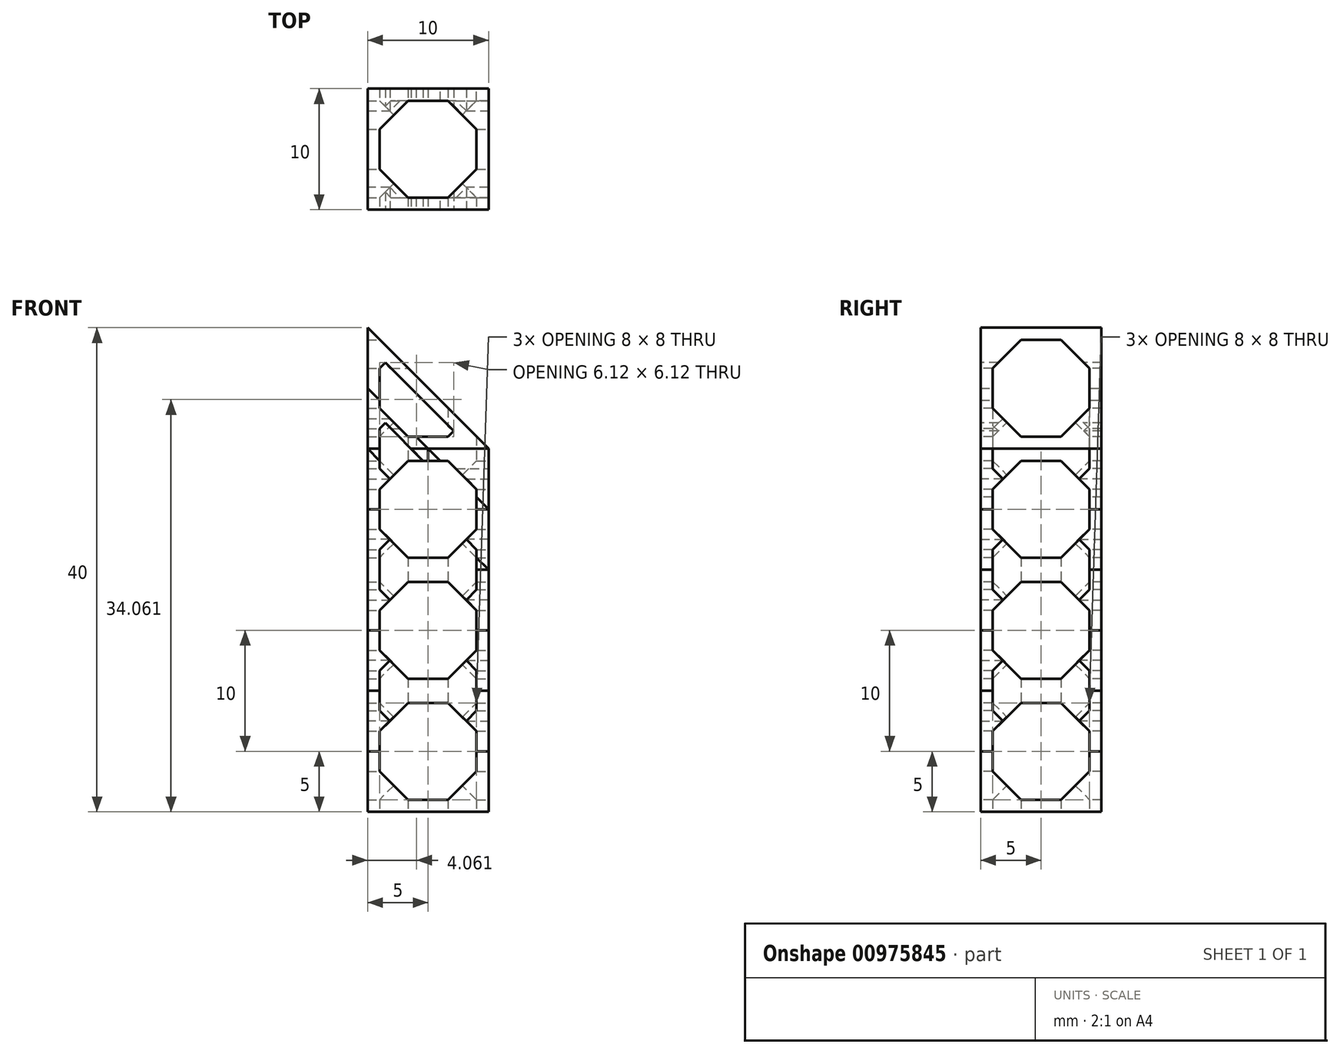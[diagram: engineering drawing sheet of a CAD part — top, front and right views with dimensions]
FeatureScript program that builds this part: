
annotation { "Feature Type Name" : "Feature", "Feature Type Description" : "" }
export const myFeature = defineFeature(function(context is Context, id is Id, definition is map)
    precondition{}
    {
        {
            var Q0;
            Q0=qCreatedBy(makeId("Front.planeOp"),FACE);
            var sketch = newSketch(context, id + "F0", { "sketchPlane" : qUnion([Q0])});
            skLineSegment(sketch, "E0.bottom", {"start": v(-5, 5) * mm, "end": v(5, 5) * mm});
            skLineSegment(sketch, "E0.top", {"start": v(-5, -5) * mm, "end": v(5, -5) * mm});
            skLineSegment(sketch, "E0.left", {"start": v(-5, 5) * mm, "end": v(-5, -5) * mm});
            skLineSegment(sketch, "E0.right", {"start": v(5, 5) * mm, "end": v(5, -5) * mm});
            skPoint(sketch, "E0.middle", {"position": v(0, 0) * mm});
            skSolve(sketch);
        }
        {
            var Q0;
            Q0=qSketchRegion(id+"F0",true);
            extrude(context, id + "F1", {"entities" : qUnion([Q0]), "endBound" : BoundingType.SYMMETRIC, "depth" : 10 * mm, "offsetDistance" : 25 * mm});
        }
        {
            var Q0;
            Q0=makeQuery(id+"F1.opExtrude","CAP_FACE",FACE,{"disambiguationData":[OSD([sQuery(id+"F0.wireOp",EDGE,"E0.bottom"),sQuery(id+"F0.wireOp",EDGE,"E0.top"),sQuery(id+"F0.wireOp",EDGE,"E0.left"),sQuery(id+"F0.wireOp",EDGE,"E0.right")])],"isStart":false});
            var sketch = newSketch(context, id + "F2", { "sketchPlane" : qUnion([Q0])});
            skCircle(sketch, "E1.cCircle", {"center": v(0, 0) * mm, "radius": 4 * mm, "construction": true});
            skLineSegment(sketch, "E1.0", {"start": v(1.66, 4) * mm, "end": v(4, 1.66) * mm});
            skLineSegment(sketch, "E1.1", {"start": v(4, 1.66) * mm, "end": v(4, -1.66) * mm});
            skLineSegment(sketch, "E1.2", {"start": v(4, -1.66) * mm, "end": v(1.66, -4) * mm});
            skLineSegment(sketch, "E1.3", {"start": v(1.66, -4) * mm, "end": v(-1.66, -4) * mm});
            skLineSegment(sketch, "E1.4", {"start": v(-1.66, -4) * mm, "end": v(-4, -1.66) * mm});
            skLineSegment(sketch, "E1.5", {"start": v(-4, -1.66) * mm, "end": v(-4, 1.66) * mm});
            skLineSegment(sketch, "E1.6", {"start": v(-4, 1.66) * mm, "end": v(-1.66, 4) * mm});
            skLineSegment(sketch, "E1.7", {"start": v(-1.66, 4) * mm, "end": v(1.66, 4) * mm});
            skPoint(sketch, "E1.0.midPoint", {"position": v(2.83, 2.83) * mm});
            skSolve(sketch);
        }
        {
            var Q0;
            Q0 = qSketchRegion(id + "F2", true);
            var Q1;
            Q1=makeQuery(id+"F1.opExtrude","CAP_FACE",FACE,{"disambiguationData":[OSD([sQuery(id+"F0.wireOp",EDGE,"E0.bottom"),sQuery(id+"F0.wireOp",EDGE,"E0.top"),sQuery(id+"F0.wireOp",EDGE,"E0.left"),sQuery(id+"F0.wireOp",EDGE,"E0.right")])],"isStart":true});
            extrude(context, id + "F3", {"entities" : qUnion([Q0]), "operationType" : NewBodyOperationType.REMOVE, "endBound" : BoundingType.UP_TO_SURFACE, "oppositeDirection" : true, "depth" : 25 * mm, "endBoundEntityFace" : qUnion([Q1]), "offsetDistance" : 25 * mm});
        }
        {
            var Q0;
            Q0=makeQuery(id+"F1.opExtrude","SWEPT_FACE",FACE,{"disambiguationData":[OSD([sQuery(id+"F0.wireOp",EDGE,"E0.right")])]});
            var sketch = newSketch(context, id + "F4", { "sketchPlane" : qUnion([Q0])});
            skCircle(sketch, "E2.cCircle", {"center": v(0, 0) * mm, "radius": 4 * mm, "construction": true});
            skLineSegment(sketch, "E2.0", {"start": v(-4, 1.66) * mm, "end": v(-1.66, 4) * mm});
            skLineSegment(sketch, "E2.1", {"start": v(-1.66, 4) * mm, "end": v(1.66, 4) * mm});
            skLineSegment(sketch, "E2.2", {"start": v(1.66, 4) * mm, "end": v(4, 1.66) * mm});
            skLineSegment(sketch, "E2.3", {"start": v(4, 1.66) * mm, "end": v(4, -1.66) * mm});
            skLineSegment(sketch, "E2.4", {"start": v(4, -1.66) * mm, "end": v(1.66, -4) * mm});
            skLineSegment(sketch, "E2.5", {"start": v(1.66, -4) * mm, "end": v(-1.66, -4) * mm});
            skLineSegment(sketch, "E2.6", {"start": v(-1.66, -4) * mm, "end": v(-4, -1.66) * mm});
            skLineSegment(sketch, "E2.7", {"start": v(-4, -1.66) * mm, "end": v(-4, 1.66) * mm});
            skPoint(sketch, "E2.0.midPoint", {"position": v(-2.83, 2.83) * mm});
            skSolve(sketch);
        }
        {
            var Q0;
            Q0 = qSketchRegion(id + "F4", true);
            var Q1;
            Q1 = qConstructionFilter(qBodyType(qCreatedBy(id + "F4" ,EDGE), BodyType.WIRE), ConstructionObject.NO);
            var Q2;
            Q2=makeQuery(id+"F1.opExtrude","SWEPT_FACE",FACE,{"disambiguationData":[OSD([sQuery(id+"F0.wireOp",EDGE,"E0.left")])]});
            extrude(context, id + "F5", {"entities" : qUnion([Q0]), "operationType" : NewBodyOperationType.REMOVE, "surfaceEntities" : qUnion([Q1]), "endBound" : BoundingType.UP_TO_SURFACE, "oppositeDirection" : true, "depth" : 25 * mm, "endBoundEntityFace" : qUnion([Q2]), "offsetDistance" : 25 * mm});
        }
        {
            var Q0;
            Q0=makeQuery(id+"F1.opExtrude","SWEPT_FACE",FACE,{"disambiguationData":[OSD([sQuery(id+"F0.wireOp",EDGE,"E0.bottom")])]});
            var sketch = newSketch(context, id + "F6", { "sketchPlane" : qUnion([Q0])});
            skCircle(sketch, "E3.cCircle", {"center": v(0, 0) * mm, "radius": 4 * mm, "construction": true});
            skLineSegment(sketch, "E3.0", {"start": v(-4, 1.66) * mm, "end": v(-1.66, 4) * mm});
            skLineSegment(sketch, "E3.1", {"start": v(-1.66, 4) * mm, "end": v(1.66, 4) * mm});
            skLineSegment(sketch, "E3.2", {"start": v(1.66, 4) * mm, "end": v(4, 1.66) * mm});
            skLineSegment(sketch, "E3.3", {"start": v(4, 1.66) * mm, "end": v(4, -1.66) * mm});
            skLineSegment(sketch, "E3.4", {"start": v(4, -1.66) * mm, "end": v(1.66, -4) * mm});
            skLineSegment(sketch, "E3.5", {"start": v(1.66, -4) * mm, "end": v(-1.66, -4) * mm});
            skLineSegment(sketch, "E3.6", {"start": v(-1.66, -4) * mm, "end": v(-4, -1.66) * mm});
            skLineSegment(sketch, "E3.7", {"start": v(-4, -1.66) * mm, "end": v(-4, 1.66) * mm});
            skPoint(sketch, "E3.0.midPoint", {"position": v(-2.83, 2.83) * mm});
            skSolve(sketch);
        }
        {
            var Q0;
            Q0 = qSketchRegion(id + "F6", true);
            var Q1;
            Q1=makeQuery(id+"F1.opExtrude","SWEPT_FACE",FACE,{"disambiguationData":[OSD([sQuery(id+"F0.wireOp",EDGE,"E0.top")])]});
            extrude(context, id + "F7", {"entities" : qUnion([Q0]), "operationType" : NewBodyOperationType.REMOVE, "endBound" : BoundingType.UP_TO_SURFACE, "oppositeDirection" : true, "depth" : 25 * mm, "endBoundEntityFace" : qUnion([Q1]), "offsetDistance" : 25 * mm});
        }
        {
            var Q0;
            Q0=qCreatedBy(makeId("Front.planeOp"),FACE);
            var sketch = newSketch(context, id + "F8", { "sketchPlane" : qUnion([Q0])});
            skLineSegment(sketch, "E4.bottom", {"start": v(-5, 10) * mm, "end": v(5, 10) * mm});
            skLineSegment(sketch, "E4.top", {"start": v(-5, -10) * mm, "end": v(5, -10) * mm});
            skLineSegment(sketch, "E4.left", {"start": v(-5, 10) * mm, "end": v(-5, -10) * mm});
            skLineSegment(sketch, "E4.right", {"start": v(5, 10) * mm, "end": v(5, -10) * mm});
            skPoint(sketch, "E4.middle", {"position": v(0, 0) * mm});
            skSolve(sketch);
        }
        {
            var Q0;
            Q0=qSketchRegion(id+"F8",true);
            extrude(context, id + "F9", {"entities" : qUnion([Q0]), "endBound" : BoundingType.SYMMETRIC, "depth" : 10 * mm, "offsetDistance" : 25 * mm});
        }
        {
            var Q0;
            Q0=makeQuery(id+"F9.opExtrude","CAP_FACE",FACE,{"disambiguationData":[OSD([sQuery(id+"F8.wireOp",EDGE,"E4.bottom"),sQuery(id+"F8.wireOp",EDGE,"E4.top"),sQuery(id+"F8.wireOp",EDGE,"E4.left"),sQuery(id+"F8.wireOp",EDGE,"E4.right")])],"isStart":false});
            var sketch = newSketch(context, id + "F10", { "sketchPlane" : qUnion([Q0])});
            skLineSegment(sketch, "E5", {"start": v(-5, 0) * mm, "end": v(5, 0) * mm, "construction": true});
            skLineSegment(sketch, "E6", {"start": v(-5, -10) * mm, "end": v(-5, 0) * mm, "construction": true});
            skLineSegment(sketch, "E7", {"start": v(-5, 10) * mm, "end": v(-5, 0) * mm, "construction": true});
            skCircle(sketch, "E8.cCircle", {"center": v(0, 5) * mm, "radius": 4 * mm, "construction": true});
            skPoint(sketch, "E8.cCircle.centerSnap0", {"position": v(-5, 5) * mm});
            skLineSegment(sketch, "E8.0", {"start": v(4, 6.66) * mm, "end": v(4, 3.34) * mm});
            skLineSegment(sketch, "E8.1", {"start": v(4, 3.34) * mm, "end": v(1.66, 1) * mm});
            skLineSegment(sketch, "E8.2", {"start": v(1.66, 1) * mm, "end": v(-1.66, 1) * mm});
            skLineSegment(sketch, "E8.3", {"start": v(-1.66, 1) * mm, "end": v(-4, 3.34) * mm});
            skLineSegment(sketch, "E8.4", {"start": v(-4, 3.34) * mm, "end": v(-4, 6.66) * mm});
            skLineSegment(sketch, "E8.5", {"start": v(-4, 6.66) * mm, "end": v(-1.66, 9) * mm});
            skLineSegment(sketch, "E8.6", {"start": v(-1.66, 9) * mm, "end": v(1.66, 9) * mm});
            skLineSegment(sketch, "E8.7", {"start": v(1.66, 9) * mm, "end": v(4, 6.66) * mm});
            skPoint(sketch, "E8.0.midPoint", {"position": v(4, 5) * mm});
            skCircle(sketch, "E9.cCircle", {"center": v(0, -5) * mm, "radius": 4 * mm, "construction": true});
            skPoint(sketch, "E9.cCircle.centerSnap0", {"position": v(-5, -5) * mm});
            skPoint(sketch, "E9.cCircle.centerSnap1", {"position": v(0, 1) * mm});
            skLineSegment(sketch, "E9.0", {"start": v(4, -3.34) * mm, "end": v(4, -6.66) * mm});
            skLineSegment(sketch, "E9.1", {"start": v(4, -6.66) * mm, "end": v(1.66, -9) * mm});
            skLineSegment(sketch, "E9.2", {"start": v(1.66, -9) * mm, "end": v(-1.66, -9) * mm});
            skLineSegment(sketch, "E9.3", {"start": v(-1.66, -9) * mm, "end": v(-4, -6.66) * mm});
            skLineSegment(sketch, "E9.4", {"start": v(-4, -6.66) * mm, "end": v(-4, -3.34) * mm});
            skLineSegment(sketch, "E9.5", {"start": v(-4, -3.34) * mm, "end": v(-1.66, -1) * mm});
            skLineSegment(sketch, "E9.6", {"start": v(-1.66, -1) * mm, "end": v(1.66, -1) * mm});
            skLineSegment(sketch, "E9.7", {"start": v(1.66, -1) * mm, "end": v(4, -3.34) * mm});
            skPoint(sketch, "E9.0.midPoint", {"position": v(4, -5) * mm});
            skSolve(sketch);
        }
        {
            var Q0;
            Q0 = qSketchRegion(id + "F10", true);
            var Q1;
            Q1=makeQuery(id+"F9.opExtrude","CAP_FACE",FACE,{"disambiguationData":[OSD([sQuery(id+"F8.wireOp",EDGE,"E4.bottom"),sQuery(id+"F8.wireOp",EDGE,"E4.top"),sQuery(id+"F8.wireOp",EDGE,"E4.left"),sQuery(id+"F8.wireOp",EDGE,"E4.right")])],"isStart":true});
            extrude(context, id + "F11", {"entities" : qUnion([Q0]), "operationType" : NewBodyOperationType.REMOVE, "endBound" : BoundingType.UP_TO_SURFACE, "oppositeDirection" : true, "depth" : 25 * mm, "endBoundEntityFace" : qUnion([Q1]), "offsetDistance" : 25 * mm});
        }
        {
            var Q0;
            Q0=makeQuery(id+"F9.opExtrude","SWEPT_FACE",FACE,{"disambiguationData":[OSD([sQuery(id+"F8.wireOp",EDGE,"E4.right")])]});
            var sketch = newSketch(context, id + "F12", { "sketchPlane" : qUnion([Q0])});
            skLineSegment(sketch, "E10", {"start": v(-5, 0) * mm, "end": v(5, 0) * mm, "construction": true});
            skLineSegment(sketch, "E11", {"start": v(-5, 10) * mm, "end": v(-5, 0) * mm, "construction": true});
            skLineSegment(sketch, "E12", {"start": v(-5, 0) * mm, "end": v(-5, -10) * mm, "construction": true});
            skCircle(sketch, "E13.cCircle", {"center": v(0, 5) * mm, "radius": 4 * mm, "construction": true});
            skPoint(sketch, "E13.cCircle.centerSnap0", {"position": v(-5, 5) * mm});
            skLineSegment(sketch, "E13.0", {"start": v(4, 6.66) * mm, "end": v(4, 3.34) * mm});
            skLineSegment(sketch, "E13.1", {"start": v(4, 3.34) * mm, "end": v(1.66, 1) * mm});
            skLineSegment(sketch, "E13.2", {"start": v(1.66, 1) * mm, "end": v(-1.66, 1) * mm});
            skLineSegment(sketch, "E13.3", {"start": v(-1.66, 1) * mm, "end": v(-4, 3.34) * mm});
            skLineSegment(sketch, "E13.4", {"start": v(-4, 3.34) * mm, "end": v(-4, 6.66) * mm});
            skLineSegment(sketch, "E13.5", {"start": v(-4, 6.66) * mm, "end": v(-1.66, 9) * mm});
            skLineSegment(sketch, "E13.6", {"start": v(-1.66, 9) * mm, "end": v(1.66, 9) * mm});
            skLineSegment(sketch, "E13.7", {"start": v(1.66, 9) * mm, "end": v(4, 6.66) * mm});
            skPoint(sketch, "E13.0.midPoint", {"position": v(4, 5) * mm});
            skCircle(sketch, "E14.cCircle", {"center": v(0, -5) * mm, "radius": 4 * mm, "construction": true});
            skPoint(sketch, "E14.cCircle.centerSnap0", {"position": v(-5, -5) * mm});
            skPoint(sketch, "E14.cCircle.centerSnap1", {"position": v(0, 1) * mm});
            skLineSegment(sketch, "E14.0", {"start": v(4, -3.34) * mm, "end": v(4, -6.66) * mm});
            skLineSegment(sketch, "E14.1", {"start": v(4, -6.66) * mm, "end": v(1.66, -9) * mm});
            skLineSegment(sketch, "E14.2", {"start": v(1.66, -9) * mm, "end": v(-1.66, -9) * mm});
            skLineSegment(sketch, "E14.3", {"start": v(-1.66, -9) * mm, "end": v(-4, -6.66) * mm});
            skLineSegment(sketch, "E14.4", {"start": v(-4, -6.66) * mm, "end": v(-4, -3.34) * mm});
            skLineSegment(sketch, "E14.5", {"start": v(-4, -3.34) * mm, "end": v(-1.66, -1) * mm});
            skLineSegment(sketch, "E14.6", {"start": v(-1.66, -1) * mm, "end": v(1.66, -1) * mm});
            skLineSegment(sketch, "E14.7", {"start": v(1.66, -1) * mm, "end": v(4, -3.34) * mm});
            skPoint(sketch, "E14.0.midPoint", {"position": v(4, -5) * mm});
            skSolve(sketch);
        }
        {
            var Q0;
            Q0 = qSketchRegion(id + "F12", true);
            var Q1;
            Q1=makeQuery(id+"F9.opExtrude","SWEPT_FACE",FACE,{"disambiguationData":[OSD([sQuery(id+"F8.wireOp",EDGE,"E4.left")])]});
            extrude(context, id + "F13", {"entities" : qUnion([Q0]), "operationType" : NewBodyOperationType.REMOVE, "endBound" : BoundingType.UP_TO_SURFACE, "oppositeDirection" : true, "depth" : 25 * mm, "endBoundEntityFace" : qUnion([Q1]), "offsetDistance" : 25 * mm});
        }
        {
            var Q0;
            Q0=makeQuery(id+"F9.opExtrude","SWEPT_FACE",FACE,{"disambiguationData":[OSD([sQuery(id+"F8.wireOp",EDGE,"E4.bottom")])]});
            var sketch = newSketch(context, id + "F14", { "sketchPlane" : qUnion([Q0])});
            skCircle(sketch, "E15.cCircle", {"center": v(0, 0) * mm, "radius": 4 * mm, "construction": true});
            skLineSegment(sketch, "E15.0", {"start": v(-4, 1.66) * mm, "end": v(-1.66, 4) * mm});
            skLineSegment(sketch, "E15.1", {"start": v(-1.66, 4) * mm, "end": v(1.66, 4) * mm});
            skLineSegment(sketch, "E15.2", {"start": v(1.66, 4) * mm, "end": v(4, 1.66) * mm});
            skLineSegment(sketch, "E15.3", {"start": v(4, 1.66) * mm, "end": v(4, -1.66) * mm});
            skLineSegment(sketch, "E15.4", {"start": v(4, -1.66) * mm, "end": v(1.66, -4) * mm});
            skLineSegment(sketch, "E15.5", {"start": v(1.66, -4) * mm, "end": v(-1.66, -4) * mm});
            skLineSegment(sketch, "E15.6", {"start": v(-1.66, -4) * mm, "end": v(-4, -1.66) * mm});
            skLineSegment(sketch, "E15.7", {"start": v(-4, -1.66) * mm, "end": v(-4, 1.66) * mm});
            skPoint(sketch, "E15.0.midPoint", {"position": v(-2.83, 2.83) * mm});
            skSolve(sketch);
        }
        {
            var Q0;
            Q0 = qSketchRegion(id + "F14", true);
            var Q1;
            Q1=makeQuery(id+"F9.opExtrude","SWEPT_FACE",FACE,{"disambiguationData":[OSD([sQuery(id+"F8.wireOp",EDGE,"E4.top")])]});
            extrude(context, id + "F15", {"entities" : qUnion([Q0]), "operationType" : NewBodyOperationType.REMOVE, "endBound" : BoundingType.UP_TO_SURFACE, "oppositeDirection" : true, "depth" : 25 * mm, "endBoundEntityFace" : qUnion([Q1]), "offsetDistance" : 25 * mm});
        }
        {
            var Q0;
            Q0=qCreatedBy(makeId("Front.planeOp"),FACE);
            var sketch = newSketch(context, id + "F16", { "sketchPlane" : qUnion([Q0])});
            skLineSegment(sketch, "E16.bottom", {"start": v(-5, 10) * mm, "end": v(0, 10) * mm});
            skLineSegment(sketch, "E16.top", {"start": v(-5, -10) * mm, "end": v(5, -10) * mm});
            skLineSegment(sketch, "E16.left", {"start": v(-5, 10) * mm, "end": v(-5, -10) * mm});
            skLineSegment(sketch, "E16.right", {"start": v(5, 0) * mm, "end": v(5, -10) * mm});
            skPoint(sketch, "E16.middle", {"position": v(0, 0) * mm});
            skLineSegment(sketch, "E17", {"start": v(0, 0) * mm, "end": v(0, 10) * mm});
            skLineSegment(sketch, "E18", {"start": v(0, 0) * mm, "end": v(5, 0) * mm});
            skSolve(sketch);
        }
        {
            var Q0;
            Q0=qSketchRegion(id+"F16",true);
            extrude(context, id + "F17", {"entities" : qUnion([Q0]), "endBound" : BoundingType.SYMMETRIC, "depth" : 10 * mm, "offsetDistance" : 25 * mm});
        }
        {
            var Q0;
            Q0=makeQuery(id+"F17.opExtrude","CAP_FACE",FACE,{"disambiguationData":[OSD([sQuery(id+"F16.wireOp",EDGE,"E16.bottom"),sQuery(id+"F16.wireOp",EDGE,"E16.top"),sQuery(id+"F16.wireOp",EDGE,"E16.left"),sQuery(id+"F16.wireOp",EDGE,"E16.right"),sQuery(id+"F16.wireOp",EDGE,"E17"),sQuery(id+"F16.wireOp",EDGE,"E18")])],"isStart":false});
            var sketch = newSketch(context, id + "F18", { "sketchPlane" : qUnion([Q0])});
            skLineSegment(sketch, "E19", {"start": v(0, 0) * mm, "end": v(-5, 0) * mm, "construction": true});
            skLineSegment(sketch, "E20", {"start": v(-5, 0) * mm, "end": v(-5, 10) * mm, "construction": true});
            skLineSegment(sketch, "E21", {"start": v(-5, 0) * mm, "end": v(-5, -10) * mm, "construction": true});
            skCircle(sketch, "E22.cCircle", {"center": v(0, -5) * mm, "radius": 4 * mm, "construction": true});
            skPoint(sketch, "E22.cCircle.centerSnap0", {"position": v(-5, -5) * mm});
            skLineSegment(sketch, "E22.0", {"start": v(4, -3.34) * mm, "end": v(4, -6.66) * mm});
            skLineSegment(sketch, "E22.1", {"start": v(4, -6.66) * mm, "end": v(1.66, -9) * mm});
            skLineSegment(sketch, "E22.2", {"start": v(1.66, -9) * mm, "end": v(-1.66, -9) * mm});
            skLineSegment(sketch, "E22.3", {"start": v(-1.66, -9) * mm, "end": v(-4, -6.66) * mm});
            skLineSegment(sketch, "E22.4", {"start": v(-4, -6.66) * mm, "end": v(-4, -3.34) * mm});
            skLineSegment(sketch, "E22.5", {"start": v(-4, -3.34) * mm, "end": v(-1.66, -1) * mm});
            skLineSegment(sketch, "E22.6", {"start": v(-1.66, -1) * mm, "end": v(1.66, -1) * mm});
            skLineSegment(sketch, "E22.7", {"start": v(1.66, -1) * mm, "end": v(4, -3.34) * mm});
            skPoint(sketch, "E22.0.midPoint", {"position": v(4, -5) * mm});
            skLineSegment(sketch, "E23.MirrorCS", {"start": v(-1.66, 1) * mm, "end": v(-1, 1) * mm});
            skLineSegment(sketch, "E24.MirrorCS", {"start": v(-4, 3.34) * mm, "end": v(-1.66, 1) * mm});
            skLineSegment(sketch, "E25.MirrorCS", {"start": v(-4, 6.66) * mm, "end": v(-4, 3.34) * mm});
            skLineSegment(sketch, "E26.MirrorCS", {"start": v(-1.66, 9) * mm, "end": v(-4, 6.66) * mm});
            skLineSegment(sketch, "E27.MirrorCS", {"start": v(-1, 9) * mm, "end": v(-1.66, 9) * mm});
            skLineSegment(sketch, "E28", {"start": v(-1, 9) * mm, "end": v(-1, 1) * mm});
            skSolve(sketch);
        }
        {
            var Q0;
            Q0 = qSketchRegion(id + "F18", true);
            var Q1;
            Q1=makeQuery(id+"F17.opExtrude","CAP_FACE",FACE,{"disambiguationData":[OSD([sQuery(id+"F16.wireOp",EDGE,"E16.bottom"),sQuery(id+"F16.wireOp",EDGE,"E16.top"),sQuery(id+"F16.wireOp",EDGE,"E16.left"),sQuery(id+"F16.wireOp",EDGE,"E16.right"),sQuery(id+"F16.wireOp",EDGE,"E17"),sQuery(id+"F16.wireOp",EDGE,"E18")])],"isStart":true});
            extrude(context, id + "F19", {"entities" : qUnion([Q0]), "operationType" : NewBodyOperationType.REMOVE, "endBound" : BoundingType.UP_TO_SURFACE, "oppositeDirection" : true, "depth" : 25 * mm, "endBoundEntityFace" : qUnion([Q1]), "offsetDistance" : 25 * mm});
        }
        {
            var Q0;
            Q0=makeQuery(id+"F17.opExtrude","SWEPT_FACE",FACE,{"disambiguationData":[OSD([sQuery(id+"F16.wireOp",EDGE,"E16.right")])]});
            var sketch = newSketch(context, id + "F20", { "sketchPlane" : qUnion([Q0])});
            skLineSegment(sketch, "E29", {"start": v(-5, -10) * mm, "end": v(-5, 0) * mm, "construction": true});
            skLineSegment(sketch, "E30", {"start": v(-5, 0) * mm, "end": v(-5, 10) * mm, "construction": true});
            skCircle(sketch, "E31.cCircle", {"center": v(0, 5) * mm, "radius": 4 * mm, "construction": true});
            skPoint(sketch, "E31.cCircle.centerSnap0", {"position": v(-5, 5) * mm});
            skLineSegment(sketch, "E31.0", {"start": v(4, 6.66) * mm, "end": v(4, 3.34) * mm});
            skLineSegment(sketch, "E31.1", {"start": v(4, 3.34) * mm, "end": v(1.66, 1) * mm});
            skLineSegment(sketch, "E31.2", {"start": v(1.66, 1) * mm, "end": v(-1.66, 1) * mm});
            skLineSegment(sketch, "E31.3", {"start": v(-1.66, 1) * mm, "end": v(-4, 3.34) * mm});
            skLineSegment(sketch, "E31.4", {"start": v(-4, 3.34) * mm, "end": v(-4, 6.66) * mm});
            skLineSegment(sketch, "E31.5", {"start": v(-4, 6.66) * mm, "end": v(-1.66, 9) * mm});
            skLineSegment(sketch, "E31.6", {"start": v(-1.66, 9) * mm, "end": v(1.66, 9) * mm});
            skLineSegment(sketch, "E31.7", {"start": v(1.66, 9) * mm, "end": v(4, 6.66) * mm});
            skPoint(sketch, "E31.0.midPoint", {"position": v(4, 5) * mm});
            skCircle(sketch, "E32.cCircle", {"center": v(0, -5) * mm, "radius": 4 * mm, "construction": true});
            skPoint(sketch, "E32.cCircle.centerSnap0", {"position": v(-5, -5) * mm});
            skLineSegment(sketch, "E32.0", {"start": v(4, -3.34) * mm, "end": v(4, -6.66) * mm});
            skLineSegment(sketch, "E32.1", {"start": v(4, -6.66) * mm, "end": v(1.66, -9) * mm});
            skLineSegment(sketch, "E32.2", {"start": v(1.66, -9) * mm, "end": v(-1.66, -9) * mm});
            skLineSegment(sketch, "E32.3", {"start": v(-1.66, -9) * mm, "end": v(-4, -6.66) * mm});
            skLineSegment(sketch, "E32.4", {"start": v(-4, -6.66) * mm, "end": v(-4, -3.34) * mm});
            skLineSegment(sketch, "E32.5", {"start": v(-4, -3.34) * mm, "end": v(-1.66, -1) * mm});
            skLineSegment(sketch, "E32.6", {"start": v(-1.66, -1) * mm, "end": v(1.66, -1) * mm});
            skLineSegment(sketch, "E32.7", {"start": v(1.66, -1) * mm, "end": v(4, -3.34) * mm});
            skPoint(sketch, "E32.0.midPoint", {"position": v(4, -5) * mm});
            skSolve(sketch);
        }
        {
            var Q0;
            Q0 = qSketchRegion(id + "F20", true);
            var Q1;
            Q1=makeQuery(id+"F17.opExtrude","SWEPT_FACE",FACE,{"disambiguationData":[OSD([sQuery(id+"F16.wireOp",EDGE,"E16.left")])]});
            extrude(context, id + "F21", {"entities" : qUnion([Q0]), "operationType" : NewBodyOperationType.REMOVE, "endBound" : BoundingType.UP_TO_SURFACE, "oppositeDirection" : true, "depth" : 25 * mm, "endBoundEntityFace" : qUnion([Q1]), "offsetDistance" : 25 * mm});
        }
        {
            var Q0;
            Q0=makeQuery(id+"F17.opExtrude","SWEPT_FACE",FACE,{"disambiguationData":[OSD([sQuery(id+"F16.wireOp",EDGE,"E16.bottom")])]});
            var sketch = newSketch(context, id + "F22", { "sketchPlane" : qUnion([Q0])});
            skLineSegment(sketch, "E33.0", {"start": v(-4, -1.66) * mm, "end": v(-4, 1.66) * mm});
            skLineSegment(sketch, "E33.1", {"start": v(-4, 1.66) * mm, "end": v(-1.66, 4) * mm});
            skLineSegment(sketch, "E33.2", {"start": v(-1.66, 4) * mm, "end": v(-1, 4) * mm});
            skLineSegment(sketch, "E33.7", {"start": v(-1.66, -4) * mm, "end": v(-4, -1.66) * mm});
            skPoint(sketch, "E33.0.midPoint", {"position": v(-4, 0) * mm});
            skLineSegment(sketch, "E34", {"start": v(-1, -4) * mm, "end": v(-1.66, -4) * mm});
            skLineSegment(sketch, "E35", {"start": v(-1, 4) * mm, "end": v(-1, -4) * mm});
            skLineSegment(sketch, "E36", {"start": v(0, 5) * mm, "end": v(0, -5) * mm, "construction": true});
            skLineSegment(sketch, "E37.MirrorCS", {"start": v(1, 4) * mm, "end": v(1, -4) * mm});
            skLineSegment(sketch, "E38.MirrorCS", {"start": v(1.66, 4) * mm, "end": v(1, 4) * mm});
            skLineSegment(sketch, "E39.MirrorCS", {"start": v(4, 1.66) * mm, "end": v(1.66, 4) * mm});
            skLineSegment(sketch, "E40.MirrorCS", {"start": v(4, -1.66) * mm, "end": v(4, 1.66) * mm});
            skLineSegment(sketch, "E41.MirrorCS", {"start": v(1.66, -4) * mm, "end": v(4, -1.66) * mm});
            skLineSegment(sketch, "E42.MirrorCS", {"start": v(1, -4) * mm, "end": v(1.66, -4) * mm});
            skSolve(sketch);
        }
        {
            var Q0;
            Q0 = qSketchRegion(id + "F22", true);
            extrude(context, id + "F23", {"entities" : qUnion([Q0]), "operationType" : NewBodyOperationType.REMOVE, "oppositeDirection" : true, "depth" : 15 * mm, "offsetDistance" : 25 * mm});
        }
        {
            var Q0;
            Q0=makeQuery(id+"F17.opExtrude","SWEPT_FACE",FACE,{"disambiguationData":[OSD([sQuery(id+"F16.wireOp",EDGE,"E16.top")])]});
            var sketch = newSketch(context, id + "F24", { "sketchPlane" : qUnion([Q0])});
            skCircle(sketch, "E43.cCircle", {"center": v(0, 0) * mm, "radius": 4 * mm, "construction": true});
            skLineSegment(sketch, "E43.0", {"start": v(4, 1.66) * mm, "end": v(4, -1.66) * mm});
            skLineSegment(sketch, "E43.1", {"start": v(4, -1.66) * mm, "end": v(1.66, -4) * mm});
            skLineSegment(sketch, "E43.2", {"start": v(1.66, -4) * mm, "end": v(-1.66, -4) * mm});
            skLineSegment(sketch, "E43.3", {"start": v(-1.66, -4) * mm, "end": v(-4, -1.66) * mm});
            skLineSegment(sketch, "E43.4", {"start": v(-4, -1.66) * mm, "end": v(-4, 1.66) * mm});
            skLineSegment(sketch, "E43.5", {"start": v(-4, 1.66) * mm, "end": v(-1.66, 4) * mm});
            skLineSegment(sketch, "E43.6", {"start": v(-1.66, 4) * mm, "end": v(1.66, 4) * mm});
            skLineSegment(sketch, "E43.7", {"start": v(1.66, 4) * mm, "end": v(4, 1.66) * mm});
            skPoint(sketch, "E43.0.midPoint", {"position": v(4, 0) * mm});
            skSolve(sketch);
        }
        {
            var Q0;
            Q0 = qSketchRegion(id + "F24", true);
            extrude(context, id + "F25", {"entities" : qUnion([Q0]), "operationType" : NewBodyOperationType.REMOVE, "oppositeDirection" : true, "depth" : 5 * mm, "offsetDistance" : 25 * mm});
        }
        {
            var Q0;
            Q0=qCreatedBy(makeId("Front.planeOp"),FACE);
            var sketch = newSketch(context, id + "F26", { "sketchPlane" : qUnion([Q0])});
            skLineSegment(sketch, "E44.top", {"start": v(5, -10) * mm, "end": v(-5, -10) * mm});
            skLineSegment(sketch, "E44.left", {"start": v(5, 0) * mm, "end": v(5, -10) * mm});
            skLineSegment(sketch, "E44.right", {"start": v(-5, 10) * mm, "end": v(-5, -10) * mm});
            skPoint(sketch, "E44.middle", {"position": v(0, 0) * mm});
            skLineSegment(sketch, "E45", {"start": v(-5, 10) * mm, "end": v(5, 0) * mm});
            skSolve(sketch);
        }
        {
            var Q0;
            Q0=qSketchRegion(id+"F26",true);
            extrude(context, id + "F27", {"entities" : qUnion([Q0]), "endBound" : BoundingType.SYMMETRIC, "depth" : 10 * mm, "offsetDistance" : 25 * mm});
        }
        {
            var Q0;
            Q0=makeQuery(id+"F27.opExtrude","CAP_FACE",FACE,{"disambiguationData":[OSD([sQuery(id+"F26.wireOp",EDGE,"E44.top"),sQuery(id+"F26.wireOp",EDGE,"E44.left"),sQuery(id+"F26.wireOp",EDGE,"E44.right"),sQuery(id+"F26.wireOp",EDGE,"E45")])],"isStart":false});
            var sketch = newSketch(context, id + "F28", { "sketchPlane" : qUnion([Q0])});
            skLineSegment(sketch, "E46", {"start": v(-5, 0) * mm, "end": v(5, 0) * mm, "construction": true});
            skLineSegment(sketch, "E47", {"start": v(-5, 0) * mm, "end": v(-5, -10) * mm, "construction": true});
            skCircle(sketch, "E48.cCircle", {"center": v(0, -5) * mm, "radius": 4 * mm, "construction": true});
            skPoint(sketch, "E48.cCircle.centerSnap0", {"position": v(-5, -5) * mm});
            skPoint(sketch, "E48.cCircle.centerSnap1", {"position": v(0, 0) * mm});
            skLineSegment(sketch, "E48.0", {"start": v(4, -3.34) * mm, "end": v(4, -6.66) * mm});
            skLineSegment(sketch, "E48.1", {"start": v(4, -6.66) * mm, "end": v(1.66, -9) * mm});
            skLineSegment(sketch, "E48.2", {"start": v(1.66, -9) * mm, "end": v(-1.66, -9) * mm});
            skLineSegment(sketch, "E48.3", {"start": v(-1.66, -9) * mm, "end": v(-4, -6.66) * mm});
            skLineSegment(sketch, "E48.4", {"start": v(-4, -6.66) * mm, "end": v(-4, -3.34) * mm});
            skLineSegment(sketch, "E48.5", {"start": v(-4, -3.34) * mm, "end": v(-1.66, -1) * mm});
            skLineSegment(sketch, "E48.6", {"start": v(-1.66, -1) * mm, "end": v(1.66, -1) * mm});
            skLineSegment(sketch, "E48.7", {"start": v(1.66, -1) * mm, "end": v(4, -3.34) * mm});
            skPoint(sketch, "E48.0.midPoint", {"position": v(4, -5) * mm});
            skLineSegment(sketch, "E49", {"start": v(-5, 0) * mm, "end": v(-5, 10) * mm, "construction": true});
            skLineSegment(sketch, "E50.2", {"start": v(1.66, 1) * mm, "end": v(-1.66, 1) * mm});
            skLineSegment(sketch, "E50.3", {"start": v(-1.66, 1) * mm, "end": v(-4, 3.34) * mm});
            skLineSegment(sketch, "E50.4", {"start": v(-4, 3.34) * mm, "end": v(-4, 6.66) * mm});
            skLineSegment(sketch, "E50.5", {"start": v(-4, 6.66) * mm, "end": v(-3.54, 7.12) * mm});
            skLineSegment(sketch, "E51", {"start": v(2.12, 1.46) * mm, "end": v(1.66, 1) * mm});
            skLineSegment(sketch, "E52", {"start": v(-3.54, 7.12) * mm, "end": v(2.12, 1.46) * mm});
            skSolve(sketch);
        }
        {
            var Q0;
            Q0 = qSketchRegion(id + "F28", true);
            var Q1;
            Q1=makeQuery(id+"F27.opExtrude","CAP_FACE",FACE,{"disambiguationData":[OSD([sQuery(id+"F26.wireOp",EDGE,"E44.top"),sQuery(id+"F26.wireOp",EDGE,"E44.left"),sQuery(id+"F26.wireOp",EDGE,"E44.right"),sQuery(id+"F26.wireOp",EDGE,"E45")])],"isStart":true});
            extrude(context, id + "F29", {"entities" : qUnion([Q0]), "operationType" : NewBodyOperationType.REMOVE, "endBound" : BoundingType.UP_TO_SURFACE, "oppositeDirection" : true, "depth" : 25 * mm, "endBoundEntityFace" : qUnion([Q1]), "offsetDistance" : 25 * mm});
        }
        {
            var Q0;
            Q0=makeQuery(id+"F27.opExtrude","SWEPT_FACE",FACE,{"disambiguationData":[OSD([sQuery(id+"F26.wireOp",EDGE,"E44.left")])]});
            var sketch = newSketch(context, id + "F30", { "sketchPlane" : qUnion([Q0])});
            skLineSegment(sketch, "E53", {"start": v(-5, 0) * mm, "end": v(-5, -10) * mm, "construction": true});
            skLineSegment(sketch, "E54", {"start": v(-5, 0) * mm, "end": v(5, 0) * mm, "construction": true});
            skLineSegment(sketch, "E55.MirrorCS", {"start": v(-5, 0) * mm, "end": v(-5, 10) * mm, "construction": true});
            skCircle(sketch, "E56.cCircle", {"center": v(0, -5) * mm, "radius": 4 * mm, "construction": true});
            skPoint(sketch, "E56.cCircle.centerSnap0", {"position": v(-5, -5) * mm});
            skLineSegment(sketch, "E56.0", {"start": v(4, -3.34) * mm, "end": v(4, -6.66) * mm});
            skLineSegment(sketch, "E56.1", {"start": v(4, -6.66) * mm, "end": v(1.66, -9) * mm});
            skLineSegment(sketch, "E56.2", {"start": v(1.66, -9) * mm, "end": v(-1.66, -9) * mm});
            skLineSegment(sketch, "E56.3", {"start": v(-1.66, -9) * mm, "end": v(-4, -6.66) * mm});
            skLineSegment(sketch, "E56.4", {"start": v(-4, -6.66) * mm, "end": v(-4, -3.34) * mm});
            skLineSegment(sketch, "E56.5", {"start": v(-4, -3.34) * mm, "end": v(-1.66, -1) * mm});
            skLineSegment(sketch, "E56.6", {"start": v(-1.66, -1) * mm, "end": v(1.66, -1) * mm});
            skLineSegment(sketch, "E56.7", {"start": v(1.66, -1) * mm, "end": v(4, -3.34) * mm});
            skPoint(sketch, "E56.0.midPoint", {"position": v(4, -5) * mm});
            skCircle(sketch, "E57.cCircle", {"center": v(0, 5) * mm, "radius": 4 * mm, "construction": true});
            skPoint(sketch, "E57.cCircle.centerSnap0", {"position": v(-5, 5) * mm});
            skLineSegment(sketch, "E57.0", {"start": v(4, 6.66) * mm, "end": v(4, 3.34) * mm});
            skLineSegment(sketch, "E57.1", {"start": v(4, 3.34) * mm, "end": v(1.66, 1) * mm});
            skLineSegment(sketch, "E57.2", {"start": v(1.66, 1) * mm, "end": v(-1.66, 1) * mm});
            skLineSegment(sketch, "E57.3", {"start": v(-1.66, 1) * mm, "end": v(-4, 3.34) * mm});
            skLineSegment(sketch, "E57.4", {"start": v(-4, 3.34) * mm, "end": v(-4, 6.66) * mm});
            skLineSegment(sketch, "E57.5", {"start": v(-4, 6.66) * mm, "end": v(-1.66, 9) * mm});
            skLineSegment(sketch, "E57.6", {"start": v(-1.66, 9) * mm, "end": v(1.66, 9) * mm});
            skLineSegment(sketch, "E57.7", {"start": v(1.66, 9) * mm, "end": v(4, 6.66) * mm});
            skPoint(sketch, "E57.0.midPoint", {"position": v(4, 5) * mm});
            skSolve(sketch);
        }
        {
            var Q0;
            Q0 = qSketchRegion(id + "F30", true);
            var Q1;
            Q1=makeQuery(id+"F27.opExtrude","SWEPT_FACE",FACE,{"disambiguationData":[OSD([sQuery(id+"F26.wireOp",EDGE,"E44.right")])]});
            extrude(context, id + "F31", {"entities" : qUnion([Q0]), "operationType" : NewBodyOperationType.REMOVE, "endBound" : BoundingType.UP_TO_SURFACE, "oppositeDirection" : true, "depth" : 25 * mm, "endBoundEntityFace" : qUnion([Q1]), "offsetDistance" : 25 * mm});
        }
        {
            var Q0;
            Q0=makeQuery(id+"F27.opExtrude","SWEPT_FACE",FACE,{"disambiguationData":[OSD([sQuery(id+"F26.wireOp",EDGE,"E44.top")])]});
            var sketch = newSketch(context, id + "F32", { "sketchPlane" : qUnion([Q0])});
            skCircle(sketch, "E58.cCircle", {"center": v(0, 0) * mm, "radius": 4 * mm, "construction": true});
            skLineSegment(sketch, "E58.0", {"start": v(-4, -1.66) * mm, "end": v(-4, 1.66) * mm});
            skLineSegment(sketch, "E58.1", {"start": v(-4, 1.66) * mm, "end": v(-1.66, 4) * mm});
            skLineSegment(sketch, "E58.2", {"start": v(-1.66, 4) * mm, "end": v(1.66, 4) * mm});
            skLineSegment(sketch, "E58.3", {"start": v(1.66, 4) * mm, "end": v(4, 1.66) * mm});
            skLineSegment(sketch, "E58.4", {"start": v(4, 1.66) * mm, "end": v(4, -1.66) * mm});
            skLineSegment(sketch, "E58.5", {"start": v(4, -1.66) * mm, "end": v(1.66, -4) * mm});
            skLineSegment(sketch, "E58.6", {"start": v(1.66, -4) * mm, "end": v(-1.66, -4) * mm});
            skLineSegment(sketch, "E58.7", {"start": v(-1.66, -4) * mm, "end": v(-4, -1.66) * mm});
            skPoint(sketch, "E58.0.midPoint", {"position": v(-4, 0) * mm});
            skSolve(sketch);
        }
        {
            var Q0;
            Q0 = qSketchRegion(id + "F32", true);
            extrude(context, id + "F33", {"entities" : qUnion([Q0]), "operationType" : NewBodyOperationType.REMOVE, "oppositeDirection" : true, "depth" : 20 * mm, "offsetDistance" : 25 * mm});
        }
        {
            var Q0;
            Q0=qCreatedBy(makeId("Front.planeOp"),FACE);
            var sketch = newSketch(context, id + "F34", { "sketchPlane" : qUnion([Q0])});
            skLineSegment(sketch, "E59.top", {"start": v(-5, -15) * mm, "end": v(5, -15) * mm});
            skLineSegment(sketch, "E59.left", {"start": v(-5, 15) * mm, "end": v(-5, -15) * mm});
            skLineSegment(sketch, "E59.right", {"start": v(5, 5) * mm, "end": v(5, -15) * mm});
            skPoint(sketch, "E59.middle", {"position": v(0, 0) * mm});
            skPoint(sketch, "E60", {"position": v(5, 5) * mm});
            skLineSegment(sketch, "E61", {"start": v(-5, 15) * mm, "end": v(5, 5) * mm});
            skSolve(sketch);
        }
        {
            var Q0;
            Q0=qSketchRegion(id+"F34",true);
            extrude(context, id + "F35", {"entities" : qUnion([Q0]), "endBound" : BoundingType.SYMMETRIC, "depth" : 10 * mm, "offsetDistance" : 25 * mm});
        }
        {
            var Q0;
            Q0=makeQuery(id+"F35.opExtrude","CAP_FACE",FACE,{"disambiguationData":[OSD([sQuery(id+"F34.wireOp",EDGE,"E59.top"),sQuery(id+"F34.wireOp",EDGE,"E59.left"),sQuery(id+"F34.wireOp",EDGE,"E59.right"),sQuery(id+"F34.wireOp",EDGE,"E61")])],"isStart":false});
            var sketch = newSketch(context, id + "F36", { "sketchPlane" : qUnion([Q0])});
            skLineSegment(sketch, "E62", {"start": v(5, 5) * mm, "end": v(-5, 5) * mm, "construction": true});
            skLineSegment(sketch, "E63", {"start": v(5, -5) * mm, "end": v(-5, -5) * mm, "construction": true});
            skLineSegment(sketch, "E64", {"start": v(5, -5) * mm, "end": v(5, -15) * mm, "construction": true});
            skLineSegment(sketch, "E65", {"start": v(-5, 15) * mm, "end": v(-5, 5) * mm, "construction": true});
            skCircle(sketch, "E66.cCircle", {"center": v(0, 0) * mm, "radius": 4 * mm, "construction": true});
            skLineSegment(sketch, "E66.0", {"start": v(-4, -1.66) * mm, "end": v(-4, 1.66) * mm});
            skLineSegment(sketch, "E66.1", {"start": v(-4, 1.66) * mm, "end": v(-1.66, 4) * mm});
            skLineSegment(sketch, "E66.2", {"start": v(-1.66, 4) * mm, "end": v(1.66, 4) * mm});
            skLineSegment(sketch, "E66.3", {"start": v(1.66, 4) * mm, "end": v(4, 1.66) * mm});
            skLineSegment(sketch, "E66.4", {"start": v(4, 1.66) * mm, "end": v(4, -1.66) * mm});
            skLineSegment(sketch, "E66.5", {"start": v(4, -1.66) * mm, "end": v(1.66, -4) * mm});
            skLineSegment(sketch, "E66.6", {"start": v(1.66, -4) * mm, "end": v(-1.66, -4) * mm});
            skLineSegment(sketch, "E66.7", {"start": v(-1.66, -4) * mm, "end": v(-4, -1.66) * mm});
            skPoint(sketch, "E66.0.midPoint", {"position": v(-4, 0) * mm});
            skCircle(sketch, "E67.cCircle", {"center": v(0, -10) * mm, "radius": 4 * mm, "construction": true});
            skPoint(sketch, "E67.cCircle.centerSnap0", {"position": v(5, -10) * mm});
            skPoint(sketch, "E67.cCircle.centerSnap1", {"position": v(0, -5) * mm});
            skLineSegment(sketch, "E67.0", {"start": v(-4, -11.66) * mm, "end": v(-4, -8.34) * mm});
            skLineSegment(sketch, "E67.1", {"start": v(-4, -8.34) * mm, "end": v(-1.66, -6) * mm});
            skLineSegment(sketch, "E67.2", {"start": v(-1.66, -6) * mm, "end": v(1.66, -6) * mm});
            skLineSegment(sketch, "E67.3", {"start": v(1.66, -6) * mm, "end": v(4, -8.34) * mm});
            skLineSegment(sketch, "E67.4", {"start": v(4, -8.34) * mm, "end": v(4, -11.66) * mm});
            skLineSegment(sketch, "E67.5", {"start": v(4, -11.66) * mm, "end": v(1.66, -14) * mm});
            skLineSegment(sketch, "E67.6", {"start": v(1.66, -14) * mm, "end": v(-1.66, -14) * mm});
            skLineSegment(sketch, "E67.7", {"start": v(-1.66, -14) * mm, "end": v(-4, -11.66) * mm});
            skPoint(sketch, "E67.0.midPoint", {"position": v(-4, -10) * mm});
            skLineSegment(sketch, "E68.0", {"start": v(-4, 8.34) * mm, "end": v(-4, 11.66) * mm});
            skLineSegment(sketch, "E68.1", {"start": v(-4, 11.66) * mm, "end": v(-3.54, 12.12) * mm});
            skLineSegment(sketch, "E68.6", {"start": v(1.66, 6) * mm, "end": v(-1.66, 6) * mm});
            skLineSegment(sketch, "E68.7", {"start": v(-1.66, 6) * mm, "end": v(-4, 8.34) * mm});
            skPoint(sketch, "E68.0.midPoint", {"position": v(-4, 10) * mm});
            skLineSegment(sketch, "E69", {"start": v(2.12, 6.46) * mm, "end": v(1.66, 6) * mm});
            skLineSegment(sketch, "E70", {"start": v(-3.54, 12.12) * mm, "end": v(2.12, 6.46) * mm});
            skSolve(sketch);
        }
        {
            var Q0;
            Q0 = qSketchRegion(id + "F36", true);
            var Q1;
            Q1=makeQuery(id+"F35.opExtrude","CAP_FACE",FACE,{"disambiguationData":[OSD([sQuery(id+"F34.wireOp",EDGE,"E59.top"),sQuery(id+"F34.wireOp",EDGE,"E59.left"),sQuery(id+"F34.wireOp",EDGE,"E59.right"),sQuery(id+"F34.wireOp",EDGE,"E61")])],"isStart":true});
            extrude(context, id + "F37", {"entities" : qUnion([Q0]), "operationType" : NewBodyOperationType.REMOVE, "endBound" : BoundingType.UP_TO_SURFACE, "oppositeDirection" : true, "depth" : 25 * mm, "endBoundEntityFace" : qUnion([Q1]), "offsetDistance" : 25 * mm});
        }
        {
            var Q0;
            Q0=makeQuery(id+"F35.opExtrude","SWEPT_FACE",FACE,{"disambiguationData":[OSD([sQuery(id+"F34.wireOp",EDGE,"E59.right")])]});
            var sketch = newSketch(context, id + "F38", { "sketchPlane" : qUnion([Q0])});
            skLineSegment(sketch, "E71", {"start": v(5, -5) * mm, "end": v(-5, -5) * mm, "construction": true});
            skLineSegment(sketch, "E72", {"start": v(-5, -5) * mm, "end": v(-5, 5) * mm, "construction": true});
            skLineSegment(sketch, "E73", {"start": v(-5, -5) * mm, "end": v(-5, -15) * mm, "construction": true});
            skLineSegment(sketch, "E74", {"start": v(-5, 5) * mm, "end": v(5, 5) * mm, "construction": true});
            skLineSegment(sketch, "E75.MirrorCS", {"start": v(-5, 15) * mm, "end": v(-5, 5) * mm, "construction": true});
            skCircle(sketch, "E76.cCircle", {"center": v(0, -10) * mm, "radius": 4 * mm, "construction": true});
            skPoint(sketch, "E76.cCircle.centerSnap0", {"position": v(-5, -10) * mm});
            skPoint(sketch, "E76.cCircle.centerSnap1", {"position": v(0, -5) * mm});
            skLineSegment(sketch, "E76.0", {"start": v(4, -8.34) * mm, "end": v(4, -11.66) * mm});
            skLineSegment(sketch, "E76.1", {"start": v(4, -11.66) * mm, "end": v(1.66, -14) * mm});
            skLineSegment(sketch, "E76.2", {"start": v(1.66, -14) * mm, "end": v(-1.66, -14) * mm});
            skLineSegment(sketch, "E76.3", {"start": v(-1.66, -14) * mm, "end": v(-4, -11.66) * mm});
            skLineSegment(sketch, "E76.4", {"start": v(-4, -11.66) * mm, "end": v(-4, -8.34) * mm});
            skLineSegment(sketch, "E76.5", {"start": v(-4, -8.34) * mm, "end": v(-1.66, -6) * mm});
            skLineSegment(sketch, "E76.6", {"start": v(-1.66, -6) * mm, "end": v(1.66, -6) * mm});
            skLineSegment(sketch, "E76.7", {"start": v(1.66, -6) * mm, "end": v(4, -8.34) * mm});
            skPoint(sketch, "E76.0.midPoint", {"position": v(4, -10) * mm});
            skCircle(sketch, "E77.cCircle", {"center": v(0, 0) * mm, "radius": 4 * mm, "construction": true});
            skLineSegment(sketch, "E77.0", {"start": v(4, 1.66) * mm, "end": v(4, -1.66) * mm});
            skLineSegment(sketch, "E77.1", {"start": v(4, -1.66) * mm, "end": v(1.66, -4) * mm});
            skLineSegment(sketch, "E77.2", {"start": v(1.66, -4) * mm, "end": v(-1.66, -4) * mm});
            skLineSegment(sketch, "E77.3", {"start": v(-1.66, -4) * mm, "end": v(-4, -1.66) * mm});
            skLineSegment(sketch, "E77.4", {"start": v(-4, -1.66) * mm, "end": v(-4, 1.66) * mm});
            skLineSegment(sketch, "E77.5", {"start": v(-4, 1.66) * mm, "end": v(-1.66, 4) * mm});
            skLineSegment(sketch, "E77.6", {"start": v(-1.66, 4) * mm, "end": v(1.66, 4) * mm});
            skLineSegment(sketch, "E77.7", {"start": v(1.66, 4) * mm, "end": v(4, 1.66) * mm});
            skPoint(sketch, "E77.0.midPoint", {"position": v(4, 0) * mm});
            skCircle(sketch, "E78.cCircle", {"center": v(0, 10) * mm, "radius": 4 * mm, "construction": true});
            skPoint(sketch, "E78.cCircle.centerSnap0", {"position": v(-5, 10) * mm});
            skLineSegment(sketch, "E78.0", {"start": v(4, 11.66) * mm, "end": v(4, 8.34) * mm});
            skLineSegment(sketch, "E78.1", {"start": v(4, 8.34) * mm, "end": v(1.66, 6) * mm});
            skLineSegment(sketch, "E78.2", {"start": v(1.66, 6) * mm, "end": v(-1.66, 6) * mm});
            skLineSegment(sketch, "E78.3", {"start": v(-1.66, 6) * mm, "end": v(-4, 8.34) * mm});
            skLineSegment(sketch, "E78.4", {"start": v(-4, 8.34) * mm, "end": v(-4, 11.66) * mm});
            skLineSegment(sketch, "E78.5", {"start": v(-4, 11.66) * mm, "end": v(-1.66, 14) * mm});
            skLineSegment(sketch, "E78.6", {"start": v(-1.66, 14) * mm, "end": v(1.66, 14) * mm});
            skLineSegment(sketch, "E78.7", {"start": v(1.66, 14) * mm, "end": v(4, 11.66) * mm});
            skPoint(sketch, "E78.0.midPoint", {"position": v(4, 10) * mm});
            skSolve(sketch);
        }
        {
            var Q0;
            Q0 = qSketchRegion(id + "F38", true);
            var Q1;
            Q1=makeQuery(id+"F35.opExtrude","SWEPT_FACE",FACE,{"disambiguationData":[OSD([sQuery(id+"F34.wireOp",EDGE,"E59.left")])]});
            extrude(context, id + "F39", {"entities" : qUnion([Q0]), "operationType" : NewBodyOperationType.REMOVE, "endBound" : BoundingType.UP_TO_SURFACE, "oppositeDirection" : true, "depth" : 25 * mm, "endBoundEntityFace" : qUnion([Q1]), "offsetDistance" : 25 * mm});
        }
        {
            var Q0;
            Q0=makeQuery(id+"F35.opExtrude","SWEPT_FACE",FACE,{"disambiguationData":[OSD([sQuery(id+"F34.wireOp",EDGE,"E59.top")])]});
            var sketch = newSketch(context, id + "F40", { "sketchPlane" : qUnion([Q0])});
            skCircle(sketch, "E79.cCircle", {"center": v(0, 0) * mm, "radius": 4 * mm, "construction": true});
            skLineSegment(sketch, "E79.0", {"start": v(4, 1.66) * mm, "end": v(4, -1.66) * mm});
            skLineSegment(sketch, "E79.1", {"start": v(4, -1.66) * mm, "end": v(1.66, -4) * mm});
            skLineSegment(sketch, "E79.2", {"start": v(1.66, -4) * mm, "end": v(-1.66, -4) * mm});
            skLineSegment(sketch, "E79.3", {"start": v(-1.66, -4) * mm, "end": v(-4, -1.66) * mm});
            skLineSegment(sketch, "E79.4", {"start": v(-4, -1.66) * mm, "end": v(-4, 1.66) * mm});
            skLineSegment(sketch, "E79.5", {"start": v(-4, 1.66) * mm, "end": v(-1.66, 4) * mm});
            skLineSegment(sketch, "E79.6", {"start": v(-1.66, 4) * mm, "end": v(1.66, 4) * mm});
            skLineSegment(sketch, "E79.7", {"start": v(1.66, 4) * mm, "end": v(4, 1.66) * mm});
            skPoint(sketch, "E79.0.midPoint", {"position": v(4, 0) * mm});
            skSolve(sketch);
        }
        {
            var Q0;
            Q0 = qSketchRegion(id + "F40", true);
            extrude(context, id + "F41", {"entities" : qUnion([Q0]), "operationType" : NewBodyOperationType.REMOVE, "oppositeDirection" : true, "depth" : 30 * mm, "offsetDistance" : 25 * mm});
        }
        {
            var Q0;
            Q0=qCreatedBy(makeId("Front.planeOp"),FACE);
            var sketch = newSketch(context, id + "F42", { "sketchPlane" : qUnion([Q0])});
            skLineSegment(sketch, "E80.top", {"start": v(-5, -20) * mm, "end": v(5, -20) * mm});
            skLineSegment(sketch, "E80.left", {"start": v(-5, 20) * mm, "end": v(-5, -20) * mm});
            skLineSegment(sketch, "E80.right", {"start": v(5, 10) * mm, "end": v(5, -20) * mm});
            skPoint(sketch, "E80.middle", {"position": v(0, 0) * mm});
            skPoint(sketch, "E81", {"position": v(5, 10) * mm});
            skLineSegment(sketch, "E82", {"start": v(-5, 20) * mm, "end": v(5, 10) * mm});
            skSolve(sketch);
        }
        {
            var Q0;
            Q0=qSketchRegion(id+"F42",true);
            extrude(context, id + "F43", {"entities" : qUnion([Q0]), "endBound" : BoundingType.SYMMETRIC, "depth" : 10 * mm, "offsetDistance" : 25 * mm});
        }
        {
            var Q0;
            Q0=makeQuery(id+"F43.opExtrude","CAP_FACE",FACE,{"disambiguationData":[OSD([sQuery(id+"F42.wireOp",EDGE,"E80.top"),sQuery(id+"F42.wireOp",EDGE,"E80.left"),sQuery(id+"F42.wireOp",EDGE,"E80.right"),sQuery(id+"F42.wireOp",EDGE,"E82")])],"isStart":false});
            var sketch = newSketch(context, id + "F44", { "sketchPlane" : qUnion([Q0])});
            skLineSegment(sketch, "E83", {"start": v(5, 10) * mm, "end": v(-5, 10) * mm, "construction": true});
            skLineSegment(sketch, "E84", {"start": v(-5, 10) * mm, "end": v(-5, 20) * mm, "construction": true});
            skLineSegment(sketch, "E85", {"start": v(-5, 0) * mm, "end": v(5, 0) * mm, "construction": true});
            skLineSegment(sketch, "E86", {"start": v(-5, 10) * mm, "end": v(-5, 0) * mm, "construction": true});
            skLineSegment(sketch, "E87.MirrorCS", {"start": v(-5, -10) * mm, "end": v(-5, 0) * mm, "construction": true});
            skLineSegment(sketch, "E88", {"start": v(-5, -10) * mm, "end": v(5, -10) * mm, "construction": true});
            skLineSegment(sketch, "E89", {"start": v(-5, -10) * mm, "end": v(-5, -20) * mm, "construction": true});
            skLineSegment(sketch, "E90.2", {"start": v(1.66, 11) * mm, "end": v(-1.66, 11) * mm});
            skLineSegment(sketch, "E90.3", {"start": v(-1.66, 11) * mm, "end": v(-4, 13.34) * mm});
            skLineSegment(sketch, "E90.4", {"start": v(-4, 13.34) * mm, "end": v(-4, 16.66) * mm});
            skLineSegment(sketch, "E90.5", {"start": v(-4, 16.66) * mm, "end": v(-3.54, 17.12) * mm});
            skCircle(sketch, "E91.cCircle", {"center": v(0, 5) * mm, "radius": 4 * mm, "construction": true});
            skPoint(sketch, "E91.cCircle.centerSnap0", {"position": v(0, 10) * mm});
            skPoint(sketch, "E91.cCircle.centerSnap1", {"position": v(-5, 5) * mm});
            skLineSegment(sketch, "E91.0", {"start": v(4, 6.66) * mm, "end": v(4, 3.34) * mm});
            skLineSegment(sketch, "E91.1", {"start": v(4, 3.34) * mm, "end": v(1.66, 1) * mm});
            skLineSegment(sketch, "E91.2", {"start": v(1.66, 1) * mm, "end": v(-1.66, 1) * mm});
            skLineSegment(sketch, "E91.3", {"start": v(-1.66, 1) * mm, "end": v(-4, 3.34) * mm});
            skLineSegment(sketch, "E91.4", {"start": v(-4, 3.34) * mm, "end": v(-4, 6.66) * mm});
            skLineSegment(sketch, "E91.5", {"start": v(-4, 6.66) * mm, "end": v(-1.66, 9) * mm});
            skLineSegment(sketch, "E91.6", {"start": v(-1.66, 9) * mm, "end": v(1.66, 9) * mm});
            skLineSegment(sketch, "E91.7", {"start": v(1.66, 9) * mm, "end": v(4, 6.66) * mm});
            skPoint(sketch, "E91.0.midPoint", {"position": v(4, 5) * mm});
            skCircle(sketch, "E92.cCircle", {"center": v(0, -5) * mm, "radius": 4 * mm, "construction": true});
            skPoint(sketch, "E92.cCircle.centerSnap0", {"position": v(-5, -5) * mm});
            skLineSegment(sketch, "E92.0", {"start": v(4, -3.34) * mm, "end": v(4, -6.66) * mm});
            skLineSegment(sketch, "E92.1", {"start": v(4, -6.66) * mm, "end": v(1.66, -9) * mm});
            skLineSegment(sketch, "E92.2", {"start": v(1.66, -9) * mm, "end": v(-1.66, -9) * mm});
            skLineSegment(sketch, "E92.3", {"start": v(-1.66, -9) * mm, "end": v(-4, -6.66) * mm});
            skLineSegment(sketch, "E92.4", {"start": v(-4, -6.66) * mm, "end": v(-4, -3.34) * mm});
            skLineSegment(sketch, "E92.5", {"start": v(-4, -3.34) * mm, "end": v(-1.66, -1) * mm});
            skLineSegment(sketch, "E92.6", {"start": v(-1.66, -1) * mm, "end": v(1.66, -1) * mm});
            skLineSegment(sketch, "E92.7", {"start": v(1.66, -1) * mm, "end": v(4, -3.34) * mm});
            skPoint(sketch, "E92.0.midPoint", {"position": v(4, -5) * mm});
            skCircle(sketch, "E93.cCircle", {"center": v(0, -15) * mm, "radius": 4 * mm, "construction": true});
            skPoint(sketch, "E93.cCircle.centerSnap0", {"position": v(0, -10) * mm});
            skPoint(sketch, "E93.cCircle.centerSnap1", {"position": v(-5, -15) * mm});
            skLineSegment(sketch, "E93.0", {"start": v(4, -13.34) * mm, "end": v(4, -16.66) * mm});
            skLineSegment(sketch, "E93.1", {"start": v(4, -16.66) * mm, "end": v(1.66, -19) * mm});
            skLineSegment(sketch, "E93.2", {"start": v(1.66, -19) * mm, "end": v(-1.66, -19) * mm});
            skLineSegment(sketch, "E93.3", {"start": v(-1.66, -19) * mm, "end": v(-4, -16.66) * mm});
            skLineSegment(sketch, "E93.4", {"start": v(-4, -16.66) * mm, "end": v(-4, -13.34) * mm});
            skLineSegment(sketch, "E93.5", {"start": v(-4, -13.34) * mm, "end": v(-1.66, -11) * mm});
            skLineSegment(sketch, "E93.6", {"start": v(-1.66, -11) * mm, "end": v(1.66, -11) * mm});
            skLineSegment(sketch, "E93.7", {"start": v(1.66, -11) * mm, "end": v(4, -13.34) * mm});
            skPoint(sketch, "E93.0.midPoint", {"position": v(4, -15) * mm});
            skLineSegment(sketch, "E94", {"start": v(2.12, 11.46) * mm, "end": v(1.66, 11) * mm});
            skLineSegment(sketch, "E95", {"start": v(-3.54, 17.12) * mm, "end": v(2.12, 11.46) * mm});
            skSolve(sketch);
        }
        {
            var Q0;
            Q0 = qSketchRegion(id + "F44", true);
            var Q1;
            Q1=makeQuery(id+"F43.opExtrude","CAP_FACE",FACE,{"disambiguationData":[OSD([sQuery(id+"F42.wireOp",EDGE,"E80.top"),sQuery(id+"F42.wireOp",EDGE,"E80.left"),sQuery(id+"F42.wireOp",EDGE,"E80.right"),sQuery(id+"F42.wireOp",EDGE,"E82")])],"isStart":true});
            extrude(context, id + "F45", {"entities" : qUnion([Q0]), "operationType" : NewBodyOperationType.REMOVE, "endBound" : BoundingType.UP_TO_SURFACE, "oppositeDirection" : true, "depth" : 25 * mm, "endBoundEntityFace" : qUnion([Q1]), "offsetDistance" : 25 * mm});
        }
        {
            var Q0;
            Q0=makeQuery(id+"F43.opExtrude","SWEPT_FACE",FACE,{"disambiguationData":[OSD([sQuery(id+"F42.wireOp",EDGE,"E80.right")])]});
            var sketch = newSketch(context, id + "F46", { "sketchPlane" : qUnion([Q0])});
            skLineSegment(sketch, "E96", {"start": v(-5, 10) * mm, "end": v(-5, 0) * mm, "construction": true});
            skLineSegment(sketch, "E97", {"start": v(-5, 0) * mm, "end": v(5, 0) * mm, "construction": true});
            skLineSegment(sketch, "E98", {"start": v(-5, 10) * mm, "end": v(5, 10) * mm, "construction": true});
            skLineSegment(sketch, "E99.MirrorCS", {"start": v(-5, 10) * mm, "end": v(-5, 20) * mm, "construction": true});
            skLineSegment(sketch, "E100.MirrorCS", {"start": v(-5, -10) * mm, "end": v(-5, 0) * mm, "construction": true});
            skLineSegment(sketch, "E101", {"start": v(-5, -10) * mm, "end": v(5, -10) * mm, "construction": true});
            skLineSegment(sketch, "E102", {"start": v(-5, -10) * mm, "end": v(-5, -20) * mm, "construction": true});
            skCircle(sketch, "E103.cCircle", {"center": v(0, 15) * mm, "radius": 4 * mm, "construction": true});
            skPoint(sketch, "E103.cCircle.centerSnap0", {"position": v(-5, 15) * mm});
            skPoint(sketch, "E103.cCircle.centerSnap1", {"position": v(0, 10) * mm});
            skLineSegment(sketch, "E103.0", {"start": v(4, 16.66) * mm, "end": v(4, 13.34) * mm});
            skLineSegment(sketch, "E103.1", {"start": v(4, 13.34) * mm, "end": v(1.66, 11) * mm});
            skLineSegment(sketch, "E103.2", {"start": v(1.66, 11) * mm, "end": v(-1.66, 11) * mm});
            skLineSegment(sketch, "E103.3", {"start": v(-1.66, 11) * mm, "end": v(-4, 13.34) * mm});
            skLineSegment(sketch, "E103.4", {"start": v(-4, 13.34) * mm, "end": v(-4, 16.66) * mm});
            skLineSegment(sketch, "E103.5", {"start": v(-4, 16.66) * mm, "end": v(-1.66, 19) * mm});
            skLineSegment(sketch, "E103.6", {"start": v(-1.66, 19) * mm, "end": v(1.66, 19) * mm});
            skLineSegment(sketch, "E103.7", {"start": v(1.66, 19) * mm, "end": v(4, 16.66) * mm});
            skPoint(sketch, "E103.0.midPoint", {"position": v(4, 15) * mm});
            skCircle(sketch, "E104.cCircle", {"center": v(0, 5) * mm, "radius": 4 * mm, "construction": true});
            skPoint(sketch, "E104.cCircle.centerSnap0", {"position": v(-5, 5) * mm});
            skLineSegment(sketch, "E104.0", {"start": v(4, 6.66) * mm, "end": v(4, 3.34) * mm});
            skLineSegment(sketch, "E104.1", {"start": v(4, 3.34) * mm, "end": v(1.66, 1) * mm});
            skLineSegment(sketch, "E104.2", {"start": v(1.66, 1) * mm, "end": v(-1.66, 1) * mm});
            skLineSegment(sketch, "E104.3", {"start": v(-1.66, 1) * mm, "end": v(-4, 3.34) * mm});
            skLineSegment(sketch, "E104.4", {"start": v(-4, 3.34) * mm, "end": v(-4, 6.66) * mm});
            skLineSegment(sketch, "E104.5", {"start": v(-4, 6.66) * mm, "end": v(-1.66, 9) * mm});
            skLineSegment(sketch, "E104.6", {"start": v(-1.66, 9) * mm, "end": v(1.66, 9) * mm});
            skLineSegment(sketch, "E104.7", {"start": v(1.66, 9) * mm, "end": v(4, 6.66) * mm});
            skPoint(sketch, "E104.0.midPoint", {"position": v(4, 5) * mm});
            skCircle(sketch, "E105.cCircle", {"center": v(0, -5) * mm, "radius": 4 * mm, "construction": true});
            skPoint(sketch, "E105.cCircle.centerSnap0", {"position": v(0, -10) * mm});
            skPoint(sketch, "E105.cCircle.centerSnap1", {"position": v(-5, -5) * mm});
            skLineSegment(sketch, "E105.0", {"start": v(4, -3.34) * mm, "end": v(4, -6.66) * mm});
            skLineSegment(sketch, "E105.1", {"start": v(4, -6.66) * mm, "end": v(1.66, -9) * mm});
            skLineSegment(sketch, "E105.2", {"start": v(1.66, -9) * mm, "end": v(-1.66, -9) * mm});
            skLineSegment(sketch, "E105.3", {"start": v(-1.66, -9) * mm, "end": v(-4, -6.66) * mm});
            skLineSegment(sketch, "E105.4", {"start": v(-4, -6.66) * mm, "end": v(-4, -3.34) * mm});
            skLineSegment(sketch, "E105.5", {"start": v(-4, -3.34) * mm, "end": v(-1.66, -1) * mm});
            skLineSegment(sketch, "E105.6", {"start": v(-1.66, -1) * mm, "end": v(1.66, -1) * mm});
            skLineSegment(sketch, "E105.7", {"start": v(1.66, -1) * mm, "end": v(4, -3.34) * mm});
            skPoint(sketch, "E105.0.midPoint", {"position": v(4, -5) * mm});
            skCircle(sketch, "E106.cCircle", {"center": v(0, -15) * mm, "radius": 4 * mm, "construction": true});
            skPoint(sketch, "E106.cCircle.centerSnap0", {"position": v(-5, -15) * mm});
            skLineSegment(sketch, "E106.0", {"start": v(4, -13.34) * mm, "end": v(4, -16.66) * mm});
            skLineSegment(sketch, "E106.1", {"start": v(4, -16.66) * mm, "end": v(1.66, -19) * mm});
            skLineSegment(sketch, "E106.2", {"start": v(1.66, -19) * mm, "end": v(-1.66, -19) * mm});
            skLineSegment(sketch, "E106.3", {"start": v(-1.66, -19) * mm, "end": v(-4, -16.66) * mm});
            skLineSegment(sketch, "E106.4", {"start": v(-4, -16.66) * mm, "end": v(-4, -13.34) * mm});
            skLineSegment(sketch, "E106.5", {"start": v(-4, -13.34) * mm, "end": v(-1.66, -11) * mm});
            skLineSegment(sketch, "E106.6", {"start": v(-1.66, -11) * mm, "end": v(1.66, -11) * mm});
            skLineSegment(sketch, "E106.7", {"start": v(1.66, -11) * mm, "end": v(4, -13.34) * mm});
            skPoint(sketch, "E106.0.midPoint", {"position": v(4, -15) * mm});
            skSolve(sketch);
        }
        {
            var Q0;
            Q0 = qSketchRegion(id + "F46", true);
            var Q1;
            Q1=makeQuery(id+"F43.opExtrude","SWEPT_FACE",FACE,{"disambiguationData":[OSD([sQuery(id+"F42.wireOp",EDGE,"E80.left")])]});
            extrude(context, id + "F47", {"entities" : qUnion([Q0]), "operationType" : NewBodyOperationType.REMOVE, "endBound" : BoundingType.UP_TO_SURFACE, "oppositeDirection" : true, "depth" : 25 * mm, "endBoundEntityFace" : qUnion([Q1]), "offsetDistance" : 25 * mm});
        }
        {
            var Q0;
            Q0=makeQuery(id+"F43.opExtrude","SWEPT_FACE",FACE,{"disambiguationData":[OSD([sQuery(id+"F42.wireOp",EDGE,"E80.top")])]});
            var sketch = newSketch(context, id + "F48", { "sketchPlane" : qUnion([Q0])});
            skCircle(sketch, "E107.cCircle", {"center": v(0, 0) * mm, "radius": 4 * mm, "construction": true});
            skLineSegment(sketch, "E107.0", {"start": v(4, 1.66) * mm, "end": v(4, -1.66) * mm});
            skLineSegment(sketch, "E107.1", {"start": v(4, -1.66) * mm, "end": v(1.66, -4) * mm});
            skLineSegment(sketch, "E107.2", {"start": v(1.66, -4) * mm, "end": v(-1.66, -4) * mm});
            skLineSegment(sketch, "E107.3", {"start": v(-1.66, -4) * mm, "end": v(-4, -1.66) * mm});
            skLineSegment(sketch, "E107.4", {"start": v(-4, -1.66) * mm, "end": v(-4, 1.66) * mm});
            skLineSegment(sketch, "E107.5", {"start": v(-4, 1.66) * mm, "end": v(-1.66, 4) * mm});
            skLineSegment(sketch, "E107.6", {"start": v(-1.66, 4) * mm, "end": v(1.66, 4) * mm});
            skLineSegment(sketch, "E107.7", {"start": v(1.66, 4) * mm, "end": v(4, 1.66) * mm});
            skPoint(sketch, "E107.0.midPoint", {"position": v(4, 0) * mm});
            skSolve(sketch);
        }
        {
            var Q0;
            Q0 = qSketchRegion(id + "F48", true);
            extrude(context, id + "F49", {"entities" : qUnion([Q0]), "operationType" : NewBodyOperationType.REMOVE, "oppositeDirection" : true, "depth" : 40 * mm, "offsetDistance" : 25 * mm});
        }
    });
